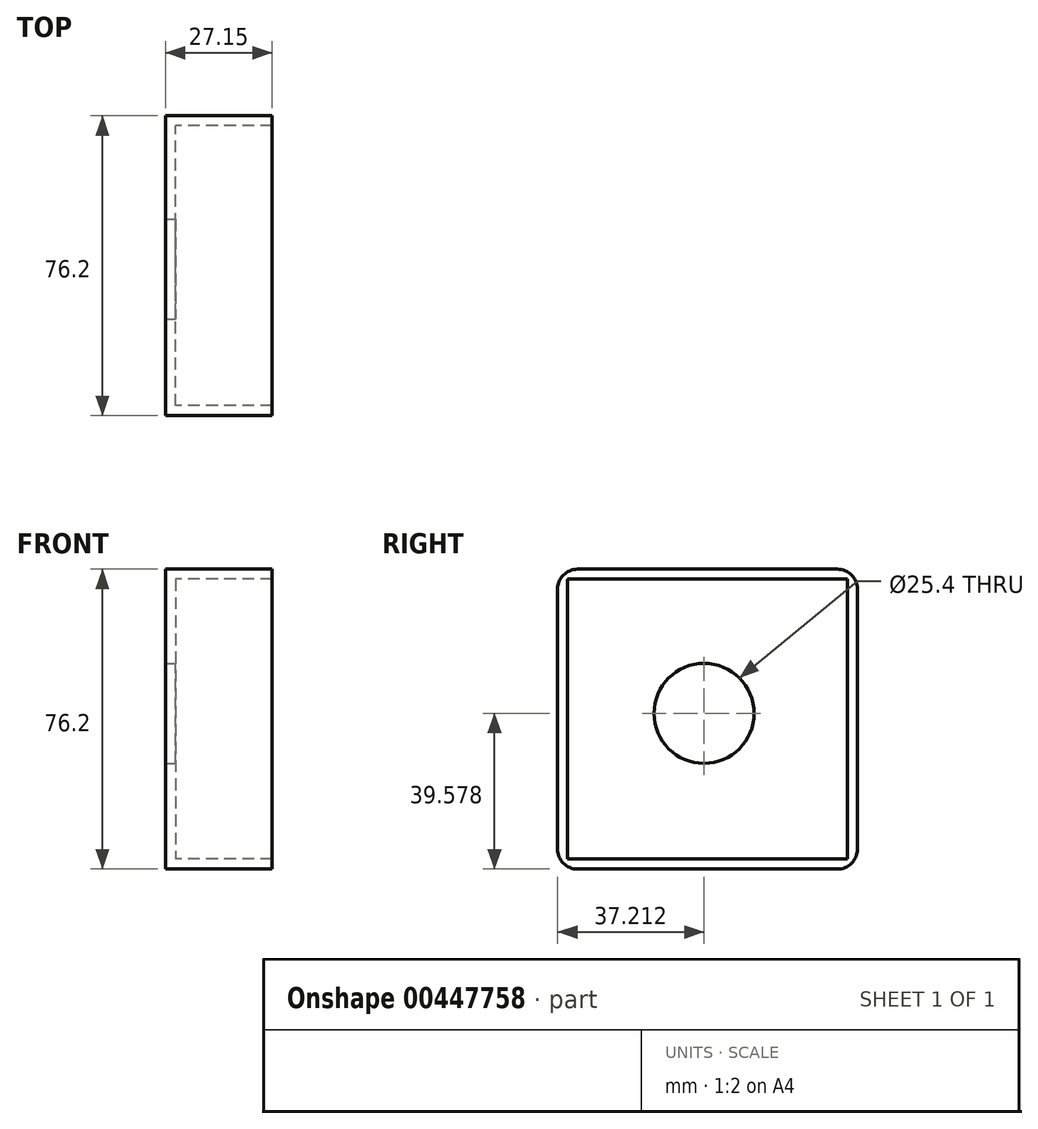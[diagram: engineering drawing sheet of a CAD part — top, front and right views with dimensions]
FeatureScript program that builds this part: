
annotation { "Feature Type Name" : "Feature", "Feature Type Description" : "" }
export const myFeature = defineFeature(function(context is Context, id is Id, definition is map)
    precondition{}
    {
        {
            var Q0;
            Q0=qCreatedBy(makeId("Right.planeOp"),FACE);
            var sketch = newSketch(context, id + "F0", { "sketchPlane" : qUnion([Q0])});
            skLineSegment(sketch, "E0.bottom", {"start": v(-66.35, 57.26) * mm, "end": v(9.85, 57.26) * mm});
            skLineSegment(sketch, "E0.top", {"start": v(-66.35, -18.94) * mm, "end": v(9.85, -18.94) * mm});
            skLineSegment(sketch, "E0.left", {"start": v(-66.35, 57.26) * mm, "end": v(-66.35, -18.94) * mm});
            skLineSegment(sketch, "E0.right", {"start": v(9.85, 57.26) * mm, "end": v(9.85, -18.94) * mm});
            skLineSegment(sketch, "E1.bottom", {"start": v(-28.25, 57.26) * mm, "end": v(9.85, 57.26) * mm});
            skLineSegment(sketch, "E1.top", {"start": v(-28.25, 57.26) * mm, "end": v(9.85, 57.26) * mm});
            skLineSegment(sketch, "E1.left", {"start": v(-28.25, 57.26) * mm, "end": v(-28.25, 57.26) * mm});
            skLineSegment(sketch, "E1.right", {"start": v(9.85, 57.26) * mm, "end": v(9.85, 57.26) * mm});
            skSolve(sketch);
        }
        {
            var Q0;
            Q0=makeQuery(id+"F0.imprint","IMPRINT",FACE,{"disambiguationData":[TD([[makeQuery(id+"F0.imprint","IMPRINT",EDGE,{"derivedFrom":sQuery(id+"F0.wireOp",EDGE,"E0.bottom")}),-1.0]])]});
            extrude(context, id + "F1", {"entities" : qUnion([Q0]), "depth" : 27.15 * mm});
        }
        {
            var Q0;
            Q0=makeQuery(id+"F1.opExtrude","CAP_FACE",FACE,{"disambiguationData":[OSD([sQuery(id+"F0.wireOp",EDGE,"E0.bottom"),sQuery(id+"F0.wireOp",EDGE,"E0.top"),sQuery(id+"F0.wireOp",EDGE,"E0.left"),sQuery(id+"F0.wireOp",EDGE,"E0.right"),sQuery(id+"F0.wireOp",EDGE,"E1.top")])],"isStart":false});
            shell(context, id + "F2", {"entities" : qUnion([Q0]), "thickness" : 2.54 * mm});
        }
        {
            var Q0;
            Q0=makeQuery(id+"F1.opExtrude","SWEPT_EDGE",EDGE,{"disambiguationData":[OSD([sQuery(id+"F0.wireOp",EDGE,"E0.top"),sQuery(id+"F0.wireOp",EDGE,"E0.right")])]});
            var Q1;
            Q1=makeQuery(id+"F1.opExtrude","SWEPT_EDGE",EDGE,{"disambiguationData":[OSD([sQuery(id+"F0.wireOp",EDGE,"E0.right"),sQuery(id+"F0.wireOp",EDGE,"E1.top")])]});
            var Q2;
            Q2=makeQuery(id+"F1.opExtrude","SWEPT_EDGE",EDGE,{"disambiguationData":[OSD([sQuery(id+"F0.wireOp",EDGE,"E0.top"),sQuery(id+"F0.wireOp",EDGE,"E0.left")])]});
            var Q3;
            Q3=makeQuery(id+"F1.opExtrude","SWEPT_EDGE",EDGE,{"disambiguationData":[OSD([sQuery(id+"F0.wireOp",EDGE,"E0.bottom"),sQuery(id+"F0.wireOp",EDGE,"E0.left")])]});
            fillet(context, id + "F3", {"entities" : qUnion([Q0, Q1, Q2, Q3]), "radius" : 5.08 * mm, "tangentPropagation" : true, "allowEdgeOverflow" : false});
        }
        {
            var Q0;
            Q0=makeQuery(id+"F2.opShell","OFFSET_FACE",FACE,{"disambiguationData":[OSD([sQuery(id+"F0.wireOp",EDGE,"E0.bottom"),sQuery(id+"F0.wireOp",EDGE,"E0.top"),sQuery(id+"F0.wireOp",EDGE,"E0.left"),sQuery(id+"F0.wireOp",EDGE,"E0.right"),sQuery(id+"F0.wireOp",EDGE,"E1.top")])]});
            var sketch = newSketch(context, id + "F4", { "sketchPlane" : qUnion([Q0])});
            skCircle(sketch, "E2", {"center": v(-29.14, 20.64) * mm, "radius": 12.7 * mm});
            skSolve(sketch);
        }
        {
            var Q0;
            Q0=makeQuery(id+"F4.imprint","IMPRINT",FACE,{"disambiguationData":[TD([[makeQuery(id+"F4.imprint","IMPRINT",EDGE,{"derivedFrom":sQuery(id+"F4.wireOp",EDGE,"E2")}),1.0]])]});
            var Q1;
            Q1=sQuery(id+"F4.wireOp",EDGE,"E2");
            extrude(context, id + "F5", {"entities" : qUnion([Q0]), "operationType" : NewBodyOperationType.REMOVE, "surfaceEntities" : qUnion([Q1]), "oppositeDirection" : true, "depth" : 51.57 * mm});
        }
    });
